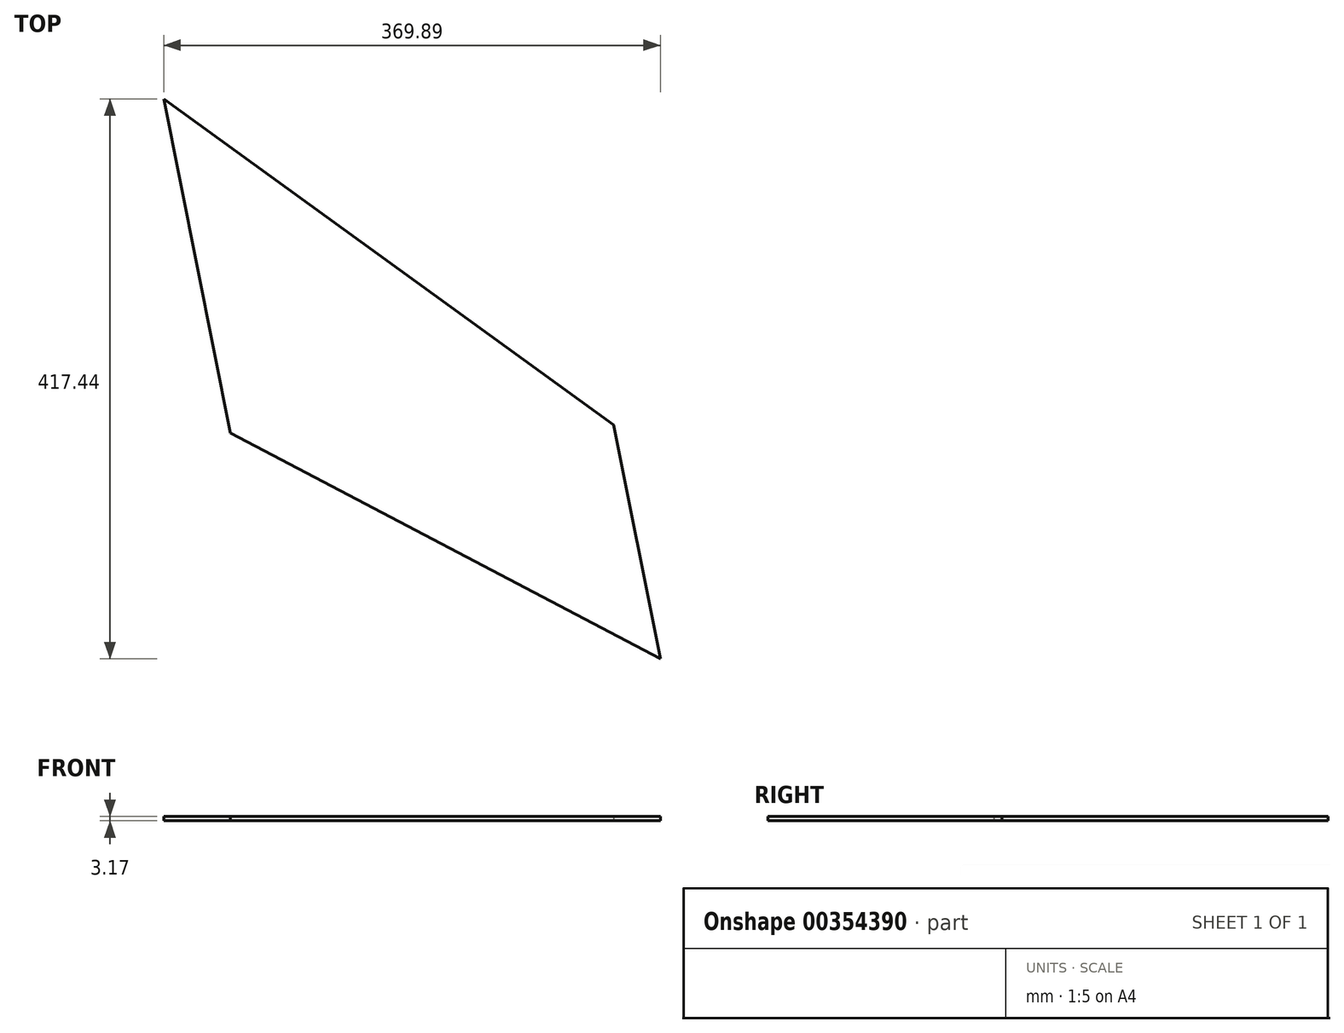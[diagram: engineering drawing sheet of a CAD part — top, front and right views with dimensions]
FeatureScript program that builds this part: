
annotation { "Feature Type Name" : "Feature", "Feature Type Description" : "" }
export const myFeature = defineFeature(function(context is Context, id is Id, definition is map)
    precondition{}
    {
        {
            var Q0;
            Q0=qCreatedBy(makeId("Top.planeOp"),FACE);
            var sketch = newSketch(context, id + "F0", { "sketchPlane" : qUnion([Q0])});
            skLineSegment(sketch, "E0", {"start": v(-218.39, 224.97) * mm, "end": v(-168.63, -24.11) * mm});
            skLineSegment(sketch, "E1", {"start": v(-168.63, -24.11) * mm, "end": v(151.5, -192.47) * mm});
            skLineSegment(sketch, "E2", {"start": v(151.5, -192.47) * mm, "end": v(116.78, -18.09) * mm});
            skLineSegment(sketch, "E3", {"start": v(116.78, -18.09) * mm, "end": v(-218.39, 224.97) * mm});
            skSolve(sketch);
        }
        {
            var Q0;
            Q0 = qSketchRegion(id + "F0", true);
            extrude(context, id + "F1", {"entities" : qUnion([Q0]), "depth" : 3.17 * mm});
        }
    });
